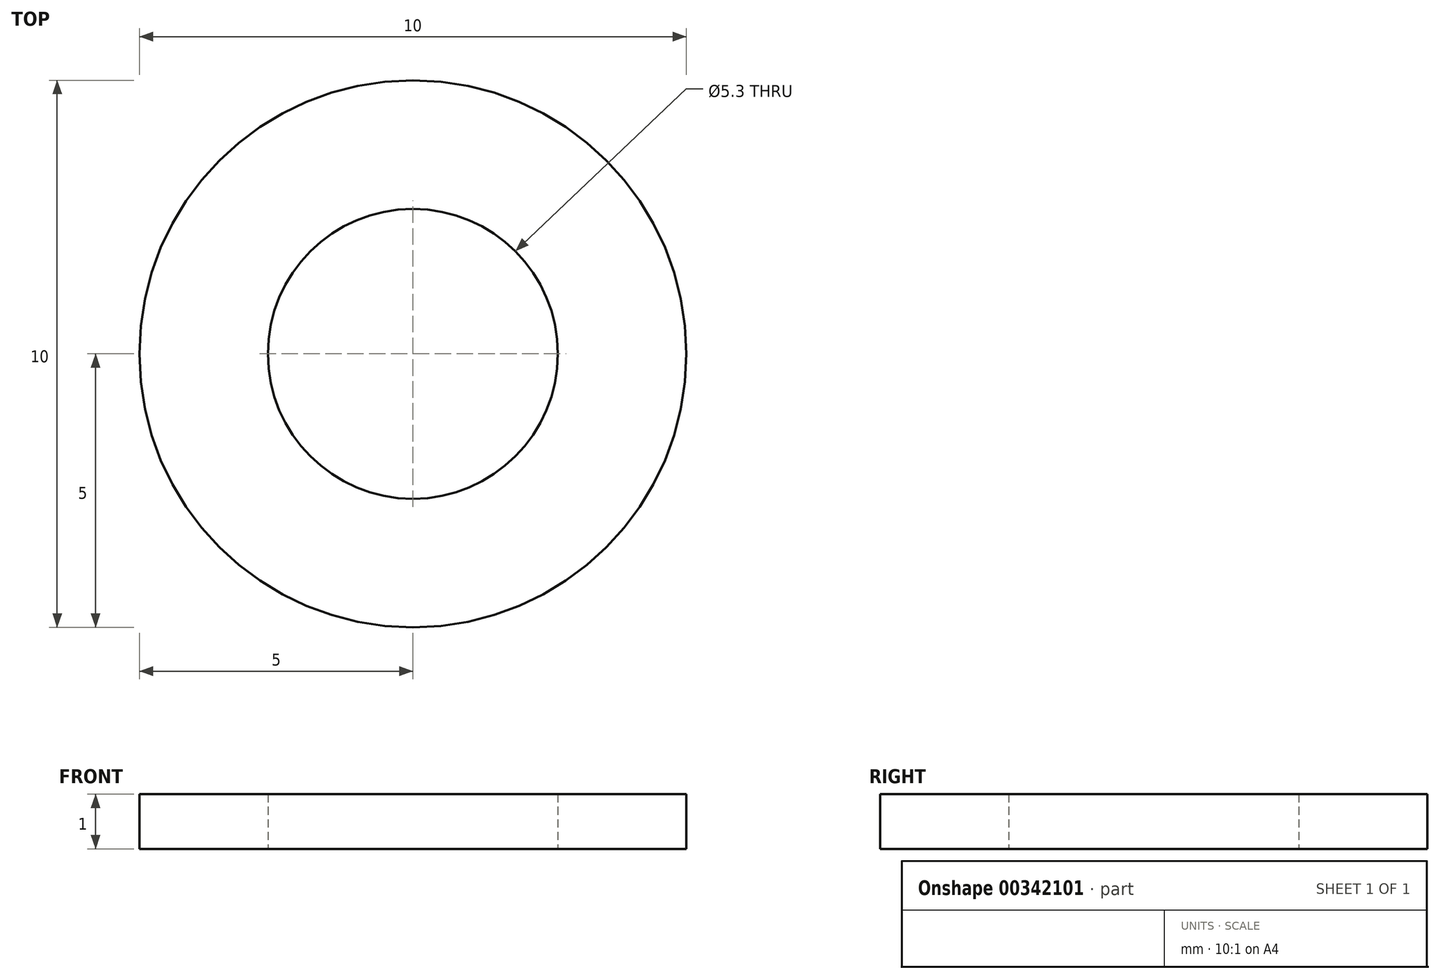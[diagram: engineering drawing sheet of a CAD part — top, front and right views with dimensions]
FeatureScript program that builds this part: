
annotation { "Feature Type Name" : "Feature", "Feature Type Description" : "" }
export const myFeature = defineFeature(function(context is Context, id is Id, definition is map)
    precondition{}
    {
        {
            var Q0;
            Q0=qCreatedBy(makeId("Top.planeOp"),FACE);
            var sketch = newSketch(context, id + "F0", { "sketchPlane" : qUnion([Q0])});
            skCircle(sketch, "E0", {"center": v(0, 0) * mm, "radius": 2.65 * mm});
            skCircle(sketch, "E1", {"center": v(0, 0) * mm, "radius": 5 * mm});
            skSolve(sketch);
        }
        {
            var Q0;
            Q0=qSketchRegion(id+"F0",true);
            extrude(context, id + "F1", {"entities" : qUnion([Q0]), "depth" : 1 * mm});
        }
    });
